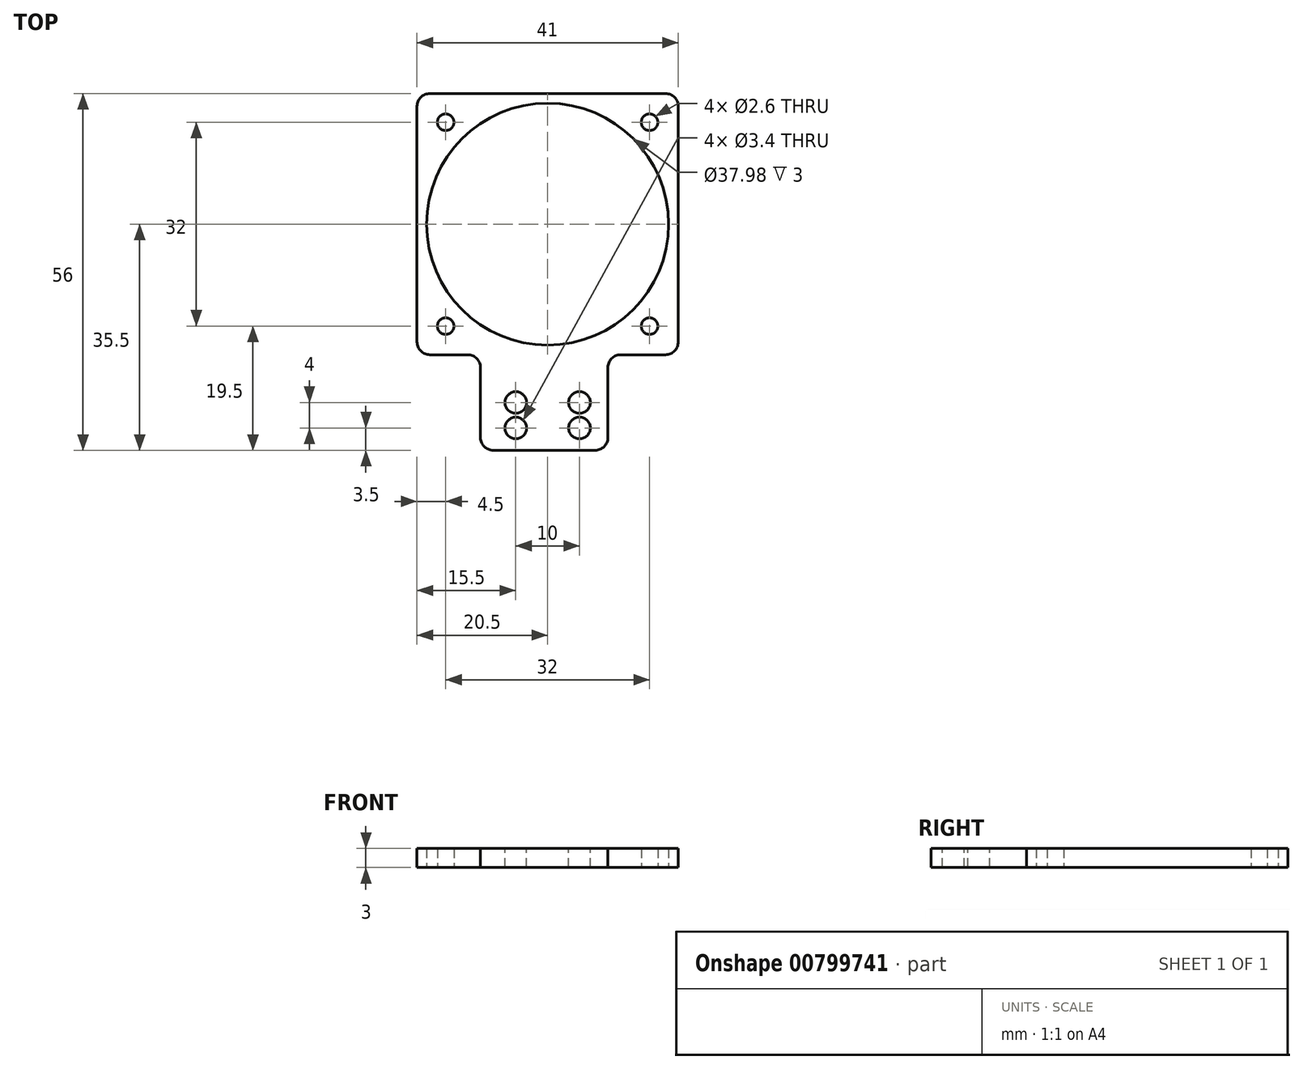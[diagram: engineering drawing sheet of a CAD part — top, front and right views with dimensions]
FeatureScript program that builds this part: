
annotation { "Feature Type Name" : "Feature", "Feature Type Description" : "" }
export const myFeature = defineFeature(function(context is Context, id is Id, definition is map)
    precondition{}
    {
        {
            var Q0;
            Q0=qCreatedBy(makeId("Top.planeOp"),FACE);
            var sketch = newSketch(context, id + "F0", { "sketchPlane" : qUnion([Q0])});
            skLineSegment(sketch, "E0.bottom", {"start": v(20.5, -20.5) * mm, "end": v(-20.5, -20.5) * mm});
            skLineSegment(sketch, "E0.top", {"start": v(20.5, 20.5) * mm, "end": v(-20.5, 20.5) * mm});
            skLineSegment(sketch, "E0.left", {"start": v(20.5, -20.5) * mm, "end": v(20.5, 20.5) * mm});
            skLineSegment(sketch, "E0.right", {"start": v(-20.5, -20.5) * mm, "end": v(-20.5, 20.5) * mm});
            skPoint(sketch, "E0.middle", {"position": v(0, 0) * mm});
            skLineSegment(sketch, "E1.bottom", {"start": v(16, -16) * mm, "end": v(-16, -16) * mm});
            skLineSegment(sketch, "E1.top", {"start": v(16, 16) * mm, "end": v(-16, 16) * mm});
            skLineSegment(sketch, "E1.left", {"start": v(16, -16) * mm, "end": v(16, 16) * mm});
            skLineSegment(sketch, "E1.right", {"start": v(-16, -16) * mm, "end": v(-16, 16) * mm});
            skCircle(sketch, "E2", {"center": v(0, 0) * mm, "radius": 18.99 * mm});
            skCircle(sketch, "E3", {"center": v(16, 16) * mm, "radius": 1.3 * mm});
            skCircle(sketch, "E4", {"center": v(-16, 16) * mm, "radius": 1.3 * mm});
            skCircle(sketch, "E5", {"center": v(16, -16) * mm, "radius": 1.3 * mm});
            skCircle(sketch, "E6", {"center": v(-16, -16) * mm, "radius": 1.3 * mm});
            skPoint(sketch, "E7", {"position": v(-10.54, -20.5) * mm});
            skPoint(sketch, "E8", {"position": v(9.46, -20.5) * mm});
            skPoint(sketch, "E9", {"position": v(-10.54, -35.5) * mm});
            skPoint(sketch, "E10", {"position": v(9.46, -35.5) * mm});
            skLineSegment(sketch, "E11", {"start": v(-10.54, -35.5) * mm, "end": v(-10.54, -20.5) * mm});
            skLineSegment(sketch, "E12", {"start": v(9.46, -20.5) * mm, "end": v(9.46, -35.5) * mm});
            skLineSegment(sketch, "E13", {"start": v(9.46, -35.5) * mm, "end": v(-10.54, -35.5) * mm});
            skPoint(sketch, "E14", {"position": v(-10.54, -28) * mm});
            skPoint(sketch, "E15", {"position": v(9.46, -28) * mm});
            skPoint(sketch, "E16", {"position": v(-0.54, -28) * mm});
            skPoint(sketch, "E16.positionSnap0", {"position": v(-0.54, -35.5) * mm});
            skPoint(sketch, "E17", {"position": v(-5, -28) * mm});
            skPoint(sketch, "E18", {"position": v(5, -28) * mm});
            skPoint(sketch, "E19", {"position": v(-5, -32) * mm});
            skPoint(sketch, "E20", {"position": v(5, -32) * mm});
            skSolve(sketch);
        }
        {
            var Q0;
            Q0=makeQuery(id+"F0.imprint","IMPRINT",FACE,{"disambiguationData":[TD([[makeQuery(id+"F0.imprint","IMPRINT",EDGE,{"derivedFrom":sQuery(id+"F0.wireOp",EDGE,"E0.top")}),1.0]])]});
            var Q1;
            {var subQ0=sQuery(id+"F0.wireOp",EDGE,"E2");var subQ1=sQuery(id+"F0.wireOp",EDGE,"E1.top");var subQ2=makeQuery(id+"F0.imprint","INTERSECT",VERTEX,{"disambiguationData":[OD(1.0)],"derivedFrom":[subQ1,subQ0]});Q1=makeQuery(id+"F0.imprint","IMPRINT",FACE,{"disambiguationData":[TD([[makeQuery(id+"F0.imprint","IMPRINT",EDGE,{"disambiguationData":[TD([[subQ2,-1.0]])],"derivedFrom":subQ1}),1.0]])]});}
            var Q2;
            {var subQ0=sQuery(id+"F0.wireOp",EDGE,"E2");var subQ1=sQuery(id+"F0.wireOp",EDGE,"E1.top");var subQ2=makeQuery(id+"F0.imprint","INTERSECT",VERTEX,{"disambiguationData":[OD(0.0)],"derivedFrom":[subQ1,subQ0]});Q2=makeQuery(id+"F0.imprint","IMPRINT",FACE,{"disambiguationData":[TD([[makeQuery(id+"F0.imprint","IMPRINT",EDGE,{"disambiguationData":[TD([[subQ2,1.0]])],"derivedFrom":subQ1}),1.0]])]});}
            var Q3;
            {var subQ0=sQuery(id+"F0.wireOp",EDGE,"E2");var subQ1=sQuery(id+"F0.wireOp",EDGE,"E1.bottom");var subQ2=makeQuery(id+"F0.imprint","INTERSECT",VERTEX,{"disambiguationData":[OD(0.0)],"derivedFrom":[subQ1,subQ0]});Q3=makeQuery(id+"F0.imprint","IMPRINT",FACE,{"disambiguationData":[TD([[makeQuery(id+"F0.imprint","IMPRINT",EDGE,{"disambiguationData":[TD([[subQ2,1.0]])],"derivedFrom":subQ1}),-1.0]])]});}
            var Q4;
            {var subQ0=sQuery(id+"F0.wireOp",EDGE,"E2");var subQ1=sQuery(id+"F0.wireOp",EDGE,"E1.bottom");var subQ2=makeQuery(id+"F0.imprint","INTERSECT",VERTEX,{"disambiguationData":[OD(1.0)],"derivedFrom":[subQ1,subQ0]});Q4=makeQuery(id+"F0.imprint","IMPRINT",FACE,{"disambiguationData":[TD([[makeQuery(id+"F0.imprint","IMPRINT",EDGE,{"disambiguationData":[TD([[subQ2,-1.0]])],"derivedFrom":subQ1}),-1.0]])]});}
            var Q5;
            {var subQ2=sQuery(id+"F0.wireOp",EDGE,"E11");Q5=makeQuery(id+"F0.imprint","IMPRINT",FACE,{"disambiguationData":[TD([[makeQuery(id+"F0.imprint","IMPRINT",EDGE,{"derivedFrom":subQ2}),-1.0]])]});}
            extrude(context, id + "F1", {"entities" : qUnion([Q0, Q1, Q2, Q3, Q4, Q5]), "depth" : 3 * mm, "offsetDistance" : 25 * mm});
        }
        {
            var Q0;
            Q0=makeQuery(id+"F1.opExtrude","SWEPT_EDGE",EDGE,{"disambiguationData":[OSD([sQuery(id+"F0.wireOp",EDGE,"E0.bottom"),sQuery(id+"F0.wireOp",EDGE,"E0.left")])]});
            var Q1;
            Q1=makeQuery(id+"F1.opExtrude","SWEPT_EDGE",EDGE,{"disambiguationData":[OSD([sQuery(id+"F0.wireOp",EDGE,"E0.top"),sQuery(id+"F0.wireOp",EDGE,"E0.left")])]});
            var Q2;
            Q2=makeQuery(id+"F1.opExtrude","SWEPT_EDGE",EDGE,{"disambiguationData":[OSD([sQuery(id+"F0.wireOp",EDGE,"E0.top"),sQuery(id+"F0.wireOp",EDGE,"E0.right")])]});
            var Q3;
            Q3=makeQuery(id+"F1.opExtrude","SWEPT_EDGE",EDGE,{"disambiguationData":[OSD([sQuery(id+"F0.wireOp",EDGE,"E0.bottom"),sQuery(id+"F0.wireOp",EDGE,"E0.right")])]});
            var Q4;
            Q4=makeQuery(id+"F1.opExtrude","SWEPT_EDGE",EDGE,{"disambiguationData":[OSD([sQuery(id+"F0.wireOp",EDGE,"E11"),sQuery(id+"F0.wireOp",EDGE,"E13")])]});
            var Q5;
            Q5=makeQuery(id+"F1.opExtrude","SWEPT_EDGE",EDGE,{"disambiguationData":[OSD([sQuery(id+"F0.wireOp",EDGE,"E12"),sQuery(id+"F0.wireOp",EDGE,"E13")])]});
            var Q6;
            Q6=makeQuery(id+"F1.opExtrude","SWEPT_EDGE",EDGE,{"disambiguationData":[OSD([sQuery(id+"F0.wireOp",EDGE,"E0.bottom"),sQuery(id+"F0.wireOp",EDGE,"E11")])]});
            var Q7;
            Q7=makeQuery(id+"F1.opExtrude","SWEPT_EDGE",EDGE,{"disambiguationData":[OSD([sQuery(id+"F0.wireOp",EDGE,"E0.bottom"),sQuery(id+"F0.wireOp",EDGE,"E12")])]});
            fillet(context, id + "F2", {"entities" : qUnion([Q0, Q1, Q2, Q3, Q4, Q5, Q6, Q7]), "tangentPropagation" : true, "radius" : 2 * mm, "defaultsChanged" : false, "vertexSettings" : [], "allowEdgeOverflow" : false});
        }
        {
            var Q0;
            Q0=sQuery(id+"F0.wireOp",VERTEX,"E17");
            var Q1;
            Q1=sQuery(id+"F0.wireOp",VERTEX,"E18");
            var Q2;
            Q2=sQuery(id+"F0.wireOp",VERTEX,"E19");
            var Q3;
            Q3=sQuery(id+"F0.wireOp",VERTEX,"E20");
            var Q4;
            Q4=makeQuery(id+"F1.opExtrude","SWEPT_BODY",BODY,{"disambiguationData":[OSD([sQuery(id+"F0.wireOp",EDGE,"E0.bottom"),sQuery(id+"F0.wireOp",EDGE,"E0.top"),sQuery(id+"F0.wireOp",EDGE,"E0.left"),sQuery(id+"F0.wireOp",EDGE,"E0.right"),sQuery(id+"F0.wireOp",EDGE,"E2"),sQuery(id+"F0.wireOp",EDGE,"E3"),sQuery(id+"F0.wireOp",EDGE,"E4"),sQuery(id+"F0.wireOp",EDGE,"E5"),sQuery(id+"F0.wireOp",EDGE,"E6"),sQuery(id+"F0.wireOp",EDGE,"E11"),sQuery(id+"F0.wireOp",EDGE,"E12"),sQuery(id+"F0.wireOp",EDGE,"E13")])]});
            hole(context, id + "F3", {"style" : HoleStyle.SIMPLE, "endStyle" : HoleEndStyle.BLIND, "oppositeDirection" : true, "holeDiameter" : 3.4 * mm, "majorDiameter" : 5 * mm, "holeDepth" : 3 * mm, "isTappedThrough" : true, "tappedDepth" : 12 * mm, "tapClearance" : 3, "startFromSketch" : true, "locations" : qUnion([Q0, Q1, Q2, Q3]), "scope" : qUnion([Q4])});
        }
    });
